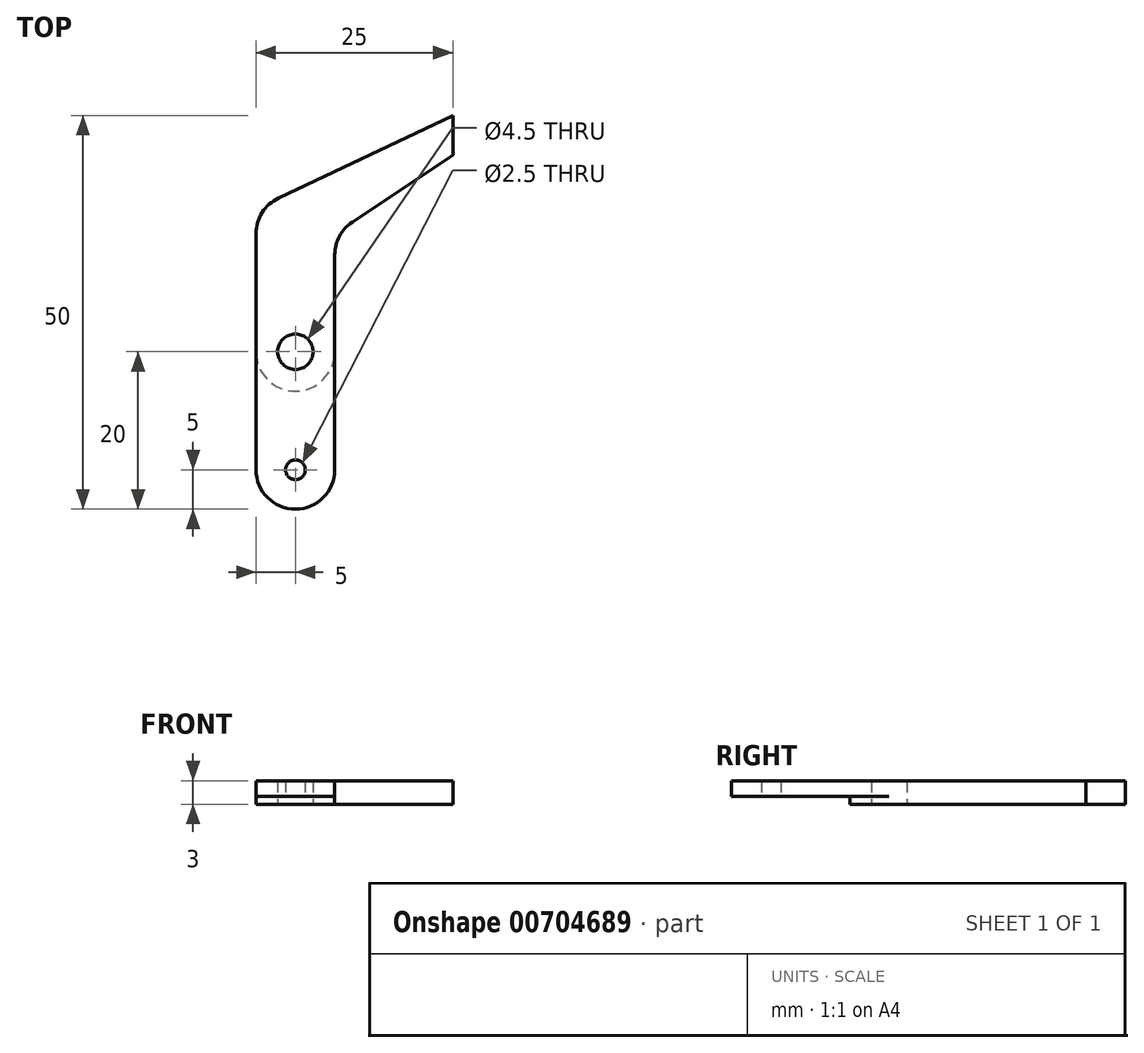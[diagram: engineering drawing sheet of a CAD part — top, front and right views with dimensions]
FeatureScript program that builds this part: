
annotation { "Feature Type Name" : "Feature", "Feature Type Description" : "" }
export const myFeature = defineFeature(function(context is Context, id is Id, definition is map)
    precondition{}
    {
        {
            var Q0;
            Q0=qCreatedBy(makeId("Top.planeOp"),FACE);
            var sketch = newSketch(context, id + "F0", { "sketchPlane" : qUnion([Q0])});
            skCircle(sketch, "E0", {"center": v(0, 0) * mm, "radius": 2.25 * mm});
            skCircle(sketch, "E1", {"center": v(0, 0) * mm, "radius": 5 * mm});
            skCircle(sketch, "E2", {"center": v(0, -15) * mm, "radius": 1.25 * mm});
            skCircle(sketch, "E3", {"center": v(0, -15) * mm, "radius": 5 * mm});
            skCircle(sketch, "E4", {"center": v(0, 15) * mm, "radius": 5 * mm});
            skLineSegment(sketch, "E5", {"start": v(-5, 15) * mm, "end": v(-5, 0) * mm});
            skLineSegment(sketch, "E6", {"start": v(-5, 0) * mm, "end": v(-5, -15) * mm});
            skLineSegment(sketch, "E7", {"start": v(5, 15) * mm, "end": v(5, 0) * mm});
            skLineSegment(sketch, "E8", {"start": v(5, 0) * mm, "end": v(5, -15) * mm});
            skLineSegment(sketch, "E9", {"start": v(-2.14, 19.52) * mm, "end": v(20, 30) * mm});
            skLineSegment(sketch, "E10", {"start": v(20, 30) * mm, "end": v(20, 25) * mm});
            skLineSegment(sketch, "E11", {"start": v(20, 25) * mm, "end": v(5, 15) * mm});
            skSolve(sketch);
        }
        {
            var Q0;
            Q0=makeQuery(id+"F0.imprint","IMPRINT",FACE,{"disambiguationData":[TD([[makeQuery(id+"F0.imprint","IMPRINT",EDGE,{"derivedFrom":sQuery(id+"F0.wireOp",EDGE,"E0")}),-1.0]])]});
            var Q1;
            {var subQ0=sQuery(id+"F0.wireOp",EDGE,"E5");Q1=makeQuery(id+"F0.imprint","IMPRINT",FACE,{"disambiguationData":[TD([[makeQuery(id+"F0.imprint","IMPRINT",EDGE,{"derivedFrom":subQ0}),1.0]])]});}
            var Q2;
            {var subQ0=sQuery(id+"F0.wireOp",EDGE,"E4");var subQ3=makeQuery(id+"F0.imprint","INTERSECT",VERTEX,{"derivedFrom":[subQ0,sQuery(id+"F0.wireOp",EDGE,"E5")]});Q2=makeQuery(id+"F0.imprint","IMPRINT",FACE,{"disambiguationData":[TD([[makeQuery(id+"F0.imprint","IMPRINT",EDGE,{"disambiguationData":[TD([[subQ3,1.0]])],"derivedFrom":subQ0}),1.0]])]});}
            var Q3;
            {var subQ2=sQuery(id+"F0.wireOp",EDGE,"E9");Q3=makeQuery(id+"F0.imprint","IMPRINT",FACE,{"disambiguationData":[TD([[makeQuery(id+"F0.imprint","IMPRINT",EDGE,{"derivedFrom":subQ2}),-1.0]])]});}
            extrude(context, id + "F1", {"entities" : qUnion([Q0, Q1, Q2, Q3]), "depth" : 3 * mm, "offsetDistance" : 25 * mm});
        }
        {
            var Q0;
            {var subQ0=sQuery(id+"F0.wireOp",EDGE,"E6");Q0=makeQuery(id+"F0.imprint","IMPRINT",FACE,{"disambiguationData":[TD([[makeQuery(id+"F0.imprint","IMPRINT",EDGE,{"derivedFrom":subQ0}),1.0]])]});}
            var Q1;
            Q1=makeQuery(id+"F0.imprint","IMPRINT",FACE,{"disambiguationData":[TD([[makeQuery(id+"F0.imprint","IMPRINT",EDGE,{"derivedFrom":sQuery(id+"F0.wireOp",EDGE,"E2")}),-1.0]])]});
            extrude(context, id + "F2", {"entities" : qUnion([Q0, Q1]), "operationType" : NewBodyOperationType.ADD, "depth" : 3 * mm, "offsetDistance" : 25 * mm, "hasSecondDirection" : true, "secondDirectionOppositeDirection" : false, "secondDirectionDepth" : 1 * mm});
        }
        {
            var Q0;
            Q0=makeQuery(id+"F1.opExtrude","SWEPT_EDGE",EDGE,{"disambiguationData":[OSD([sQuery(id+"F0.wireOp",EDGE,"E4"),sQuery(id+"F0.wireOp",EDGE,"E7"),sQuery(id+"F0.wireOp",EDGE,"E11")])]});
            fillet(context, id + "F3", {"entities" : qUnion([Q0]), "radius" : 5 * mm, "tangentPropagation" : true, "allowEdgeOverflow" : false});
        }
    });
